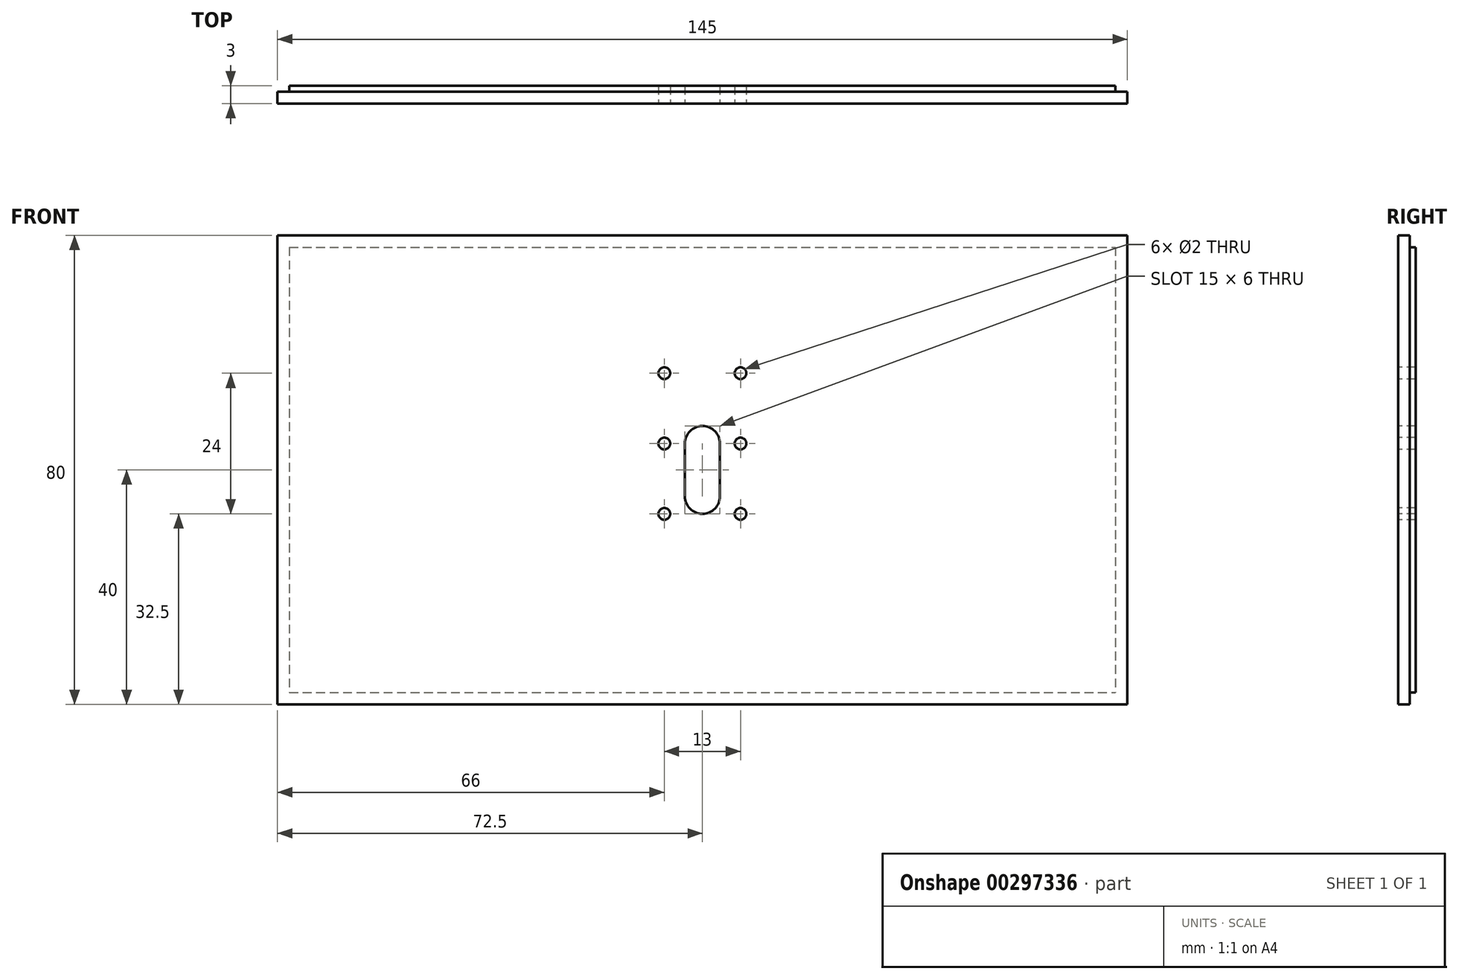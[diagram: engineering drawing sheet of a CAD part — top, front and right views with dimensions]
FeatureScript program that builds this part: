
annotation { "Feature Type Name" : "Feature", "Feature Type Description" : "" }
export const myFeature = defineFeature(function(context is Context, id is Id, definition is map)
    precondition{}
    {
        {
            var Q0;
            Q0=qCreatedBy(makeId("Front.planeOp"),FACE);
            var sketch = newSketch(context, id + "F0", { "sketchPlane" : qUnion([Q0])});
            skLineSegment(sketch, "E0.bottom", {"start": v(72.5, 40) * mm, "end": v(-72.5, 40) * mm});
            skLineSegment(sketch, "E0.top", {"start": v(72.5, -40) * mm, "end": v(-72.5, -40) * mm});
            skLineSegment(sketch, "E0.left", {"start": v(72.5, 40) * mm, "end": v(72.5, -40) * mm});
            skLineSegment(sketch, "E0.right", {"start": v(-72.5, 40) * mm, "end": v(-72.5, -40) * mm});
            skPoint(sketch, "E0.middle", {"position": v(0, 0) * mm});
            skSolve(sketch);
        }
        {
            var Q0;
            Q0 = qSketchRegion(id + "F0", true);
            extrude(context, id + "F1", {"entities" : qUnion([Q0]), "depth" : 2 * mm});
        }
        {
            var Q0;
            Q0=makeQuery(id+"F1.opExtrude","CAP_FACE",FACE,{"disambiguationData":[OSD([sQuery(id+"F0.wireOp",EDGE,"E0.bottom"),sQuery(id+"F0.wireOp",EDGE,"E0.top"),sQuery(id+"F0.wireOp",EDGE,"E0.left"),sQuery(id+"F0.wireOp",EDGE,"E0.right")])],"isStart":true});
            var sketch = newSketch(context, id + "F2", { "sketchPlane" : qUnion([Q0])});
            skLineSegment(sketch, "E1.bottom", {"start": v(70.5, 38) * mm, "end": v(-70.5, 38) * mm});
            skLineSegment(sketch, "E1.top", {"start": v(70.5, -38) * mm, "end": v(-70.5, -38) * mm});
            skLineSegment(sketch, "E1.left", {"start": v(70.5, 38) * mm, "end": v(70.5, -38) * mm});
            skLineSegment(sketch, "E1.right", {"start": v(-70.5, 38) * mm, "end": v(-70.5, -38) * mm});
            skPoint(sketch, "E1.middle", {"position": v(0, 0) * mm});
            skSolve(sketch);
        }
        {
            var Q0;
            Q0 = qSketchRegion(id + "F2", true);
            extrude(context, id + "F3", {"entities" : qUnion([Q0]), "operationType" : NewBodyOperationType.ADD, "depth" : 1 * mm});
        }
        {
            var Q0;
            Q0=makeQuery(id+"F1.opExtrude","CAP_FACE",FACE,{"disambiguationData":[OSD([sQuery(id+"F0.wireOp",EDGE,"E0.bottom"),sQuery(id+"F0.wireOp",EDGE,"E0.top"),sQuery(id+"F0.wireOp",EDGE,"E0.left"),sQuery(id+"F0.wireOp",EDGE,"E0.right")])],"isStart":false});
            var sketch = newSketch(context, id + "F4", { "sketchPlane" : qUnion([Q0])});
            skLineSegment(sketch, "E2.left", {"start": v(3, 4.5) * mm, "end": v(3, -4.5) * mm});
            skLineSegment(sketch, "E2.right", {"start": v(-3, 4.5) * mm, "end": v(-3, -4.5) * mm});
            skPoint(sketch, "E2.middle", {"position": v(0, 0) * mm});
            skArc(sketch, "E3", {"start": v(3, 4.5) * mm, "mid": v(0, 7.5) * mm, "end": v(-3, 4.5) * mm});
            skArc(sketch, "E4", {"start": v(-3, -4.5) * mm, "mid": v(0, -7.5) * mm, "end": v(3, -4.5) * mm});
            skSolve(sketch);
        }
        {
            var Q0;
            Q0 = qSketchRegion(id + "F4", true);
            extrude(context, id + "F5", {"entities" : qUnion([Q0]), "operationType" : NewBodyOperationType.REMOVE, "oppositeDirection" : true, "depth" : 25 * mm});
        }
        {
            var Q0;
            Q0=makeQuery(id+"F1.opExtrude","CAP_FACE",FACE,{"disambiguationData":[OSD([sQuery(id+"F0.wireOp",EDGE,"E0.bottom"),sQuery(id+"F0.wireOp",EDGE,"E0.top"),sQuery(id+"F0.wireOp",EDGE,"E0.left"),sQuery(id+"F0.wireOp",EDGE,"E0.right")])],"isStart":false});
            var sketch = newSketch(context, id + "F6", { "sketchPlane" : qUnion([Q0])});
            skLineSegment(sketch, "E5.bottom", {"start": v(-6.5, 16.5) * mm, "end": v(6.5, 16.5) * mm, "construction": true});
            skLineSegment(sketch, "E5.top", {"start": v(-6.5, -7.5) * mm, "end": v(6.5, -7.5) * mm, "construction": true});
            skLineSegment(sketch, "E5.left", {"start": v(-6.5, 16.5) * mm, "end": v(-6.5, -7.5) * mm, "construction": true});
            skLineSegment(sketch, "E5.right", {"start": v(6.5, 16.5) * mm, "end": v(6.5, -7.5) * mm, "construction": true});
            skCircle(sketch, "E6", {"center": v(-6.5, 16.5) * mm, "radius": 1 * mm});
            skCircle(sketch, "E7", {"center": v(6.5, 16.5) * mm, "radius": 1 * mm});
            skCircle(sketch, "E8", {"center": v(6.5, -7.5) * mm, "radius": 1 * mm});
            skCircle(sketch, "E9", {"center": v(-6.5, -7.5) * mm, "radius": 1 * mm});
            skCircle(sketch, "E10", {"center": v(-6.5, 4.5) * mm, "radius": 1 * mm});
            skCircle(sketch, "E11", {"center": v(6.5, 4.5) * mm, "radius": 1 * mm});
            skSolve(sketch);
        }
        {
            var Q0;
            Q0 = qSketchRegion(id + "F6", true);
            extrude(context, id + "F7", {"entities" : qUnion([Q0]), "operationType" : NewBodyOperationType.REMOVE, "oppositeDirection" : true, "depth" : 25 * mm});
        }
    });
